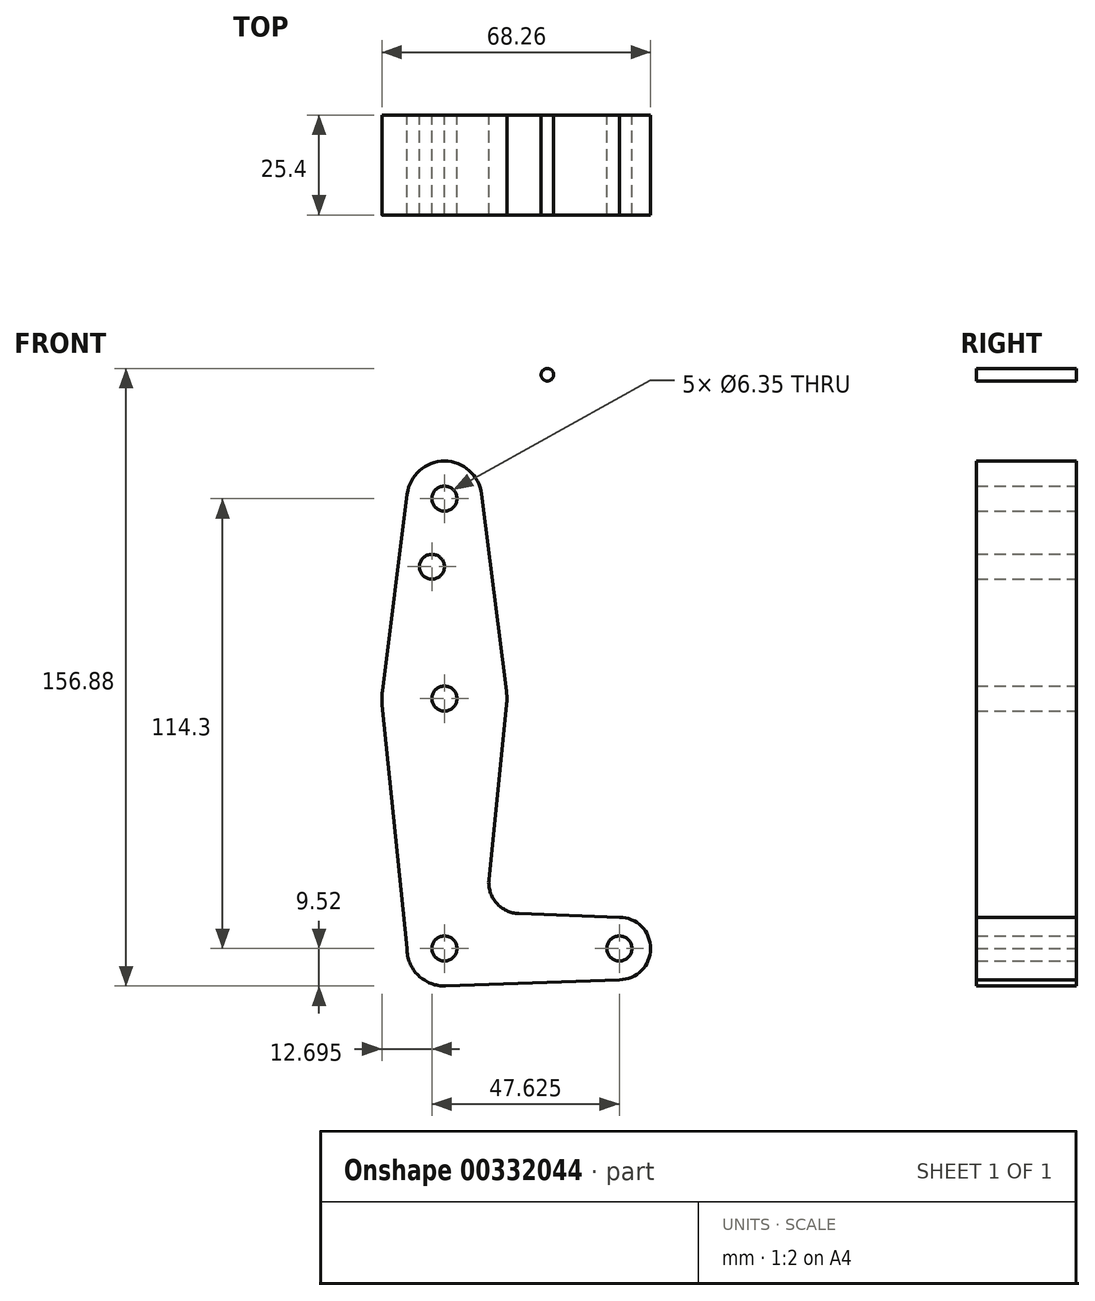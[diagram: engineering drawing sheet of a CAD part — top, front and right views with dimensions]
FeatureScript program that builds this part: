
annotation { "Feature Type Name" : "Feature", "Feature Type Description" : "" }
export const myFeature = defineFeature(function(context is Context, id is Id, definition is map)
    precondition{}
    {
        {
            var Q0;
            Q0=qCreatedBy(makeId("Front.planeOp"),FACE);
            var sketch = newSketch(context, id + "F0", { "sketchPlane" : qUnion([Q0])});
            skLineSegment(sketch, "E0", {"start": v(0, 114.3) * mm, "end": v(0, 0) * mm, "construction": true});
            skLineSegment(sketch, "E1", {"start": v(0, 0) * mm, "end": v(44.45, 0) * mm, "construction": true});
            skCircle(sketch, "E2", {"center": v(0, 114.3) * mm, "radius": 9.53 * mm});
            skCircle(sketch, "E3", {"center": v(0, 63.5) * mm, "radius": 15.88 * mm});
            skCircle(sketch, "E4", {"center": v(0, 0) * mm, "radius": 9.53 * mm});
            skCircle(sketch, "E5", {"center": v(44.45, 0) * mm, "radius": 7.94 * mm});
            skLineSegment(sketch, "E6", {"start": v(-9.53, 0) * mm, "end": v(-15.8, 61.9) * mm});
            skLineSegment(sketch, "E7", {"start": v(11.3, 17.6) * mm, "end": v(15.8, 61.9) * mm});
            skLineSegment(sketch, "E8", {"start": v(44.45, 7.94) * mm, "end": v(18.93, 8.85) * mm});
            skLineSegment(sketch, "E9", {"start": v(44.45, -7.94) * mm, "end": v(0, -9.53) * mm});
            skLineSegment(sketch, "E10", {"start": v(-15.75, 65.48) * mm, "end": v(-9.45, 115.5) * mm});
            skLineSegment(sketch, "E11", {"start": v(15.75, 65.48) * mm, "end": v(9.45, 115.5) * mm});
            skCircle(sketch, "E12", {"center": v(0, 114.3) * mm, "radius": 3.18 * mm});
            skCircle(sketch, "E13", {"center": v(26.14, 145.77) * mm, "radius": 1.59 * mm});
            skCircle(sketch, "E14", {"center": v(0, 0) * mm, "radius": 3.18 * mm});
            skCircle(sketch, "E15", {"center": v(44.45, 0) * mm, "radius": 3.18 * mm});
            skPoint(sketch, "E16.newPointB", {"position": v(0, 9.53) * mm});
            skArc(sketch, "E16.filletArc", {"start": v(11.3, 17.6) * mm, "mid": v(13.22, 11.57) * mm, "end": v(18.93, 8.85) * mm});
            skCircle(sketch, "E17", {"center": v(0, 63.5) * mm, "radius": 3.18 * mm});
            skCircle(sketch, "E18", {"center": v(-3.18, 97) * mm, "radius": 3.18 * mm});
            skSolve(sketch);
        }
        {
            var Q0;
            Q0 = qSketchRegion(id + "F0", true);
            extrude(context, id + "F1", {"entities" : qUnion([Q0]), "depth" : 25.4 * mm});
        }
    });
